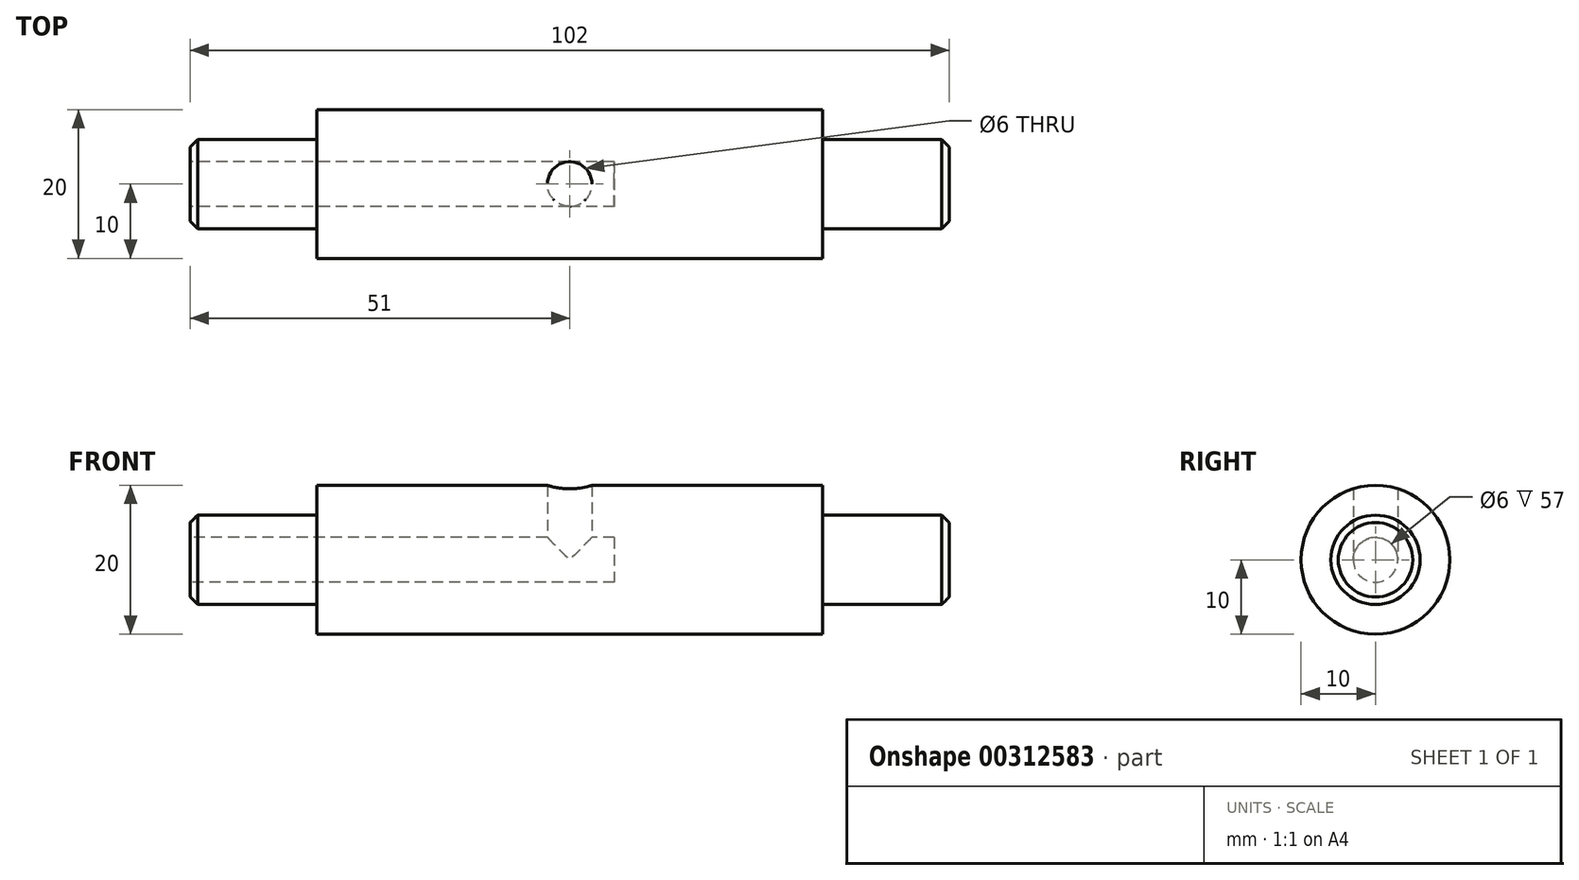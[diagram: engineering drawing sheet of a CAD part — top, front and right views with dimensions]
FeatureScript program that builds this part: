
annotation { "Feature Type Name" : "Feature", "Feature Type Description" : "" }
export const myFeature = defineFeature(function(context is Context, id is Id, definition is map)
    precondition{}
    {
        {
            var Q0;
            Q0=qCreatedBy(makeId("Front.planeOp"),FACE);
            var sketch = newSketch(context, id + "F0", { "sketchPlane" : qUnion([Q0])});
            skLineSegment(sketch, "E0", {"start": v(-51, 0) * mm, "end": v(51, 0) * mm});
            skLineSegment(sketch, "E1", {"start": v(-51, 0) * mm, "end": v(-51, 6) * mm});
            skLineSegment(sketch, "E2", {"start": v(-51, 6) * mm, "end": v(-34, 6) * mm});
            skLineSegment(sketch, "E3", {"start": v(-34, 6) * mm, "end": v(-34, 10) * mm});
            skLineSegment(sketch, "E4", {"start": v(-34, 10) * mm, "end": v(34, 10) * mm});
            skLineSegment(sketch, "E5", {"start": v(34, 10) * mm, "end": v(34, 6) * mm});
            skLineSegment(sketch, "E6", {"start": v(34, 6) * mm, "end": v(51, 6) * mm});
            skLineSegment(sketch, "E7", {"start": v(51, 6) * mm, "end": v(51, 0) * mm});
            skSolve(sketch);
        }
        {
            var Q0;
            Q0=makeQuery(id+"F0.imprint","IMPRINT",FACE,{"disambiguationData":[TD([[makeQuery(id+"F0.imprint","IMPRINT",EDGE,{"derivedFrom":sQuery(id+"F0.wireOp",EDGE,"E0")}),1.0]])]});
            var Q1;
            Q1=sQuery(id+"F0.wireOp",EDGE,"E0");
            revolve(context, id + "F1", {"entities" : qUnion([Q0]), "axis" : qUnion([Q1]), "revolveType" : RevolveType.FULL});
        }
        {
            var Q0;
            Q0=makeQuery(id+"F1.opRevolve","SWEPT_EDGE",EDGE,{"disambiguationData":[OSD([sQuery(id+"F0.wireOp",EDGE,"E6"),sQuery(id+"F0.wireOp",EDGE,"E7")])]});
            var Q1;
            Q1=makeQuery(id+"F1.opRevolve","SWEPT_EDGE",EDGE,{"disambiguationData":[OSD([sQuery(id+"F0.wireOp",EDGE,"E1"),sQuery(id+"F0.wireOp",EDGE,"E2")])]});
            chamfer(context, id + "F2", {"entities" : qUnion([Q0, Q1]), "width" : 1 * mm, "tangentPropagation" : true});
        }
        {
            var Q0;
            Q0=makeQuery(id+"F1.opRevolve","SWEPT_FACE",FACE,{"disambiguationData":[OSD([sQuery(id+"F0.wireOp",EDGE,"E1")])]});
            var sketch = newSketch(context, id + "F3", { "sketchPlane" : qUnion([Q0])});
            skCircle(sketch, "E8", {"center": v(0, 0) * mm, "radius": 3 * mm});
            skSolve(sketch);
        }
        {
            var Q0;
            Q0=makeQuery(id+"F3.imprint","IMPRINT",FACE,{"disambiguationData":[TD([[makeQuery(id+"F3.imprint","IMPRINT",EDGE,{"derivedFrom":sQuery(id+"F3.wireOp",EDGE,"E8")}),1.0]])]});
            extrude(context, id + "F4", {"entities" : qUnion([Q0]), "operationType" : NewBodyOperationType.REMOVE, "oppositeDirection" : true, "depth" : 57 * mm});
        }
        {
            var Q0;
            Q0=qCreatedBy(makeId("Top.planeOp"),FACE);
            var sketch = newSketch(context, id + "F5", { "sketchPlane" : qUnion([Q0])});
            skCircle(sketch, "E9", {"center": v(0, 0) * mm, "radius": 3 * mm});
            skSolve(sketch);
        }
        {
            var Q0;
            Q0 = qSketchRegion(id + "F5", true);
            extrude(context, id + "F6", {"entities" : qUnion([Q0]), "operationType" : NewBodyOperationType.REMOVE, "depth" : 32 * mm});
        }
    });
